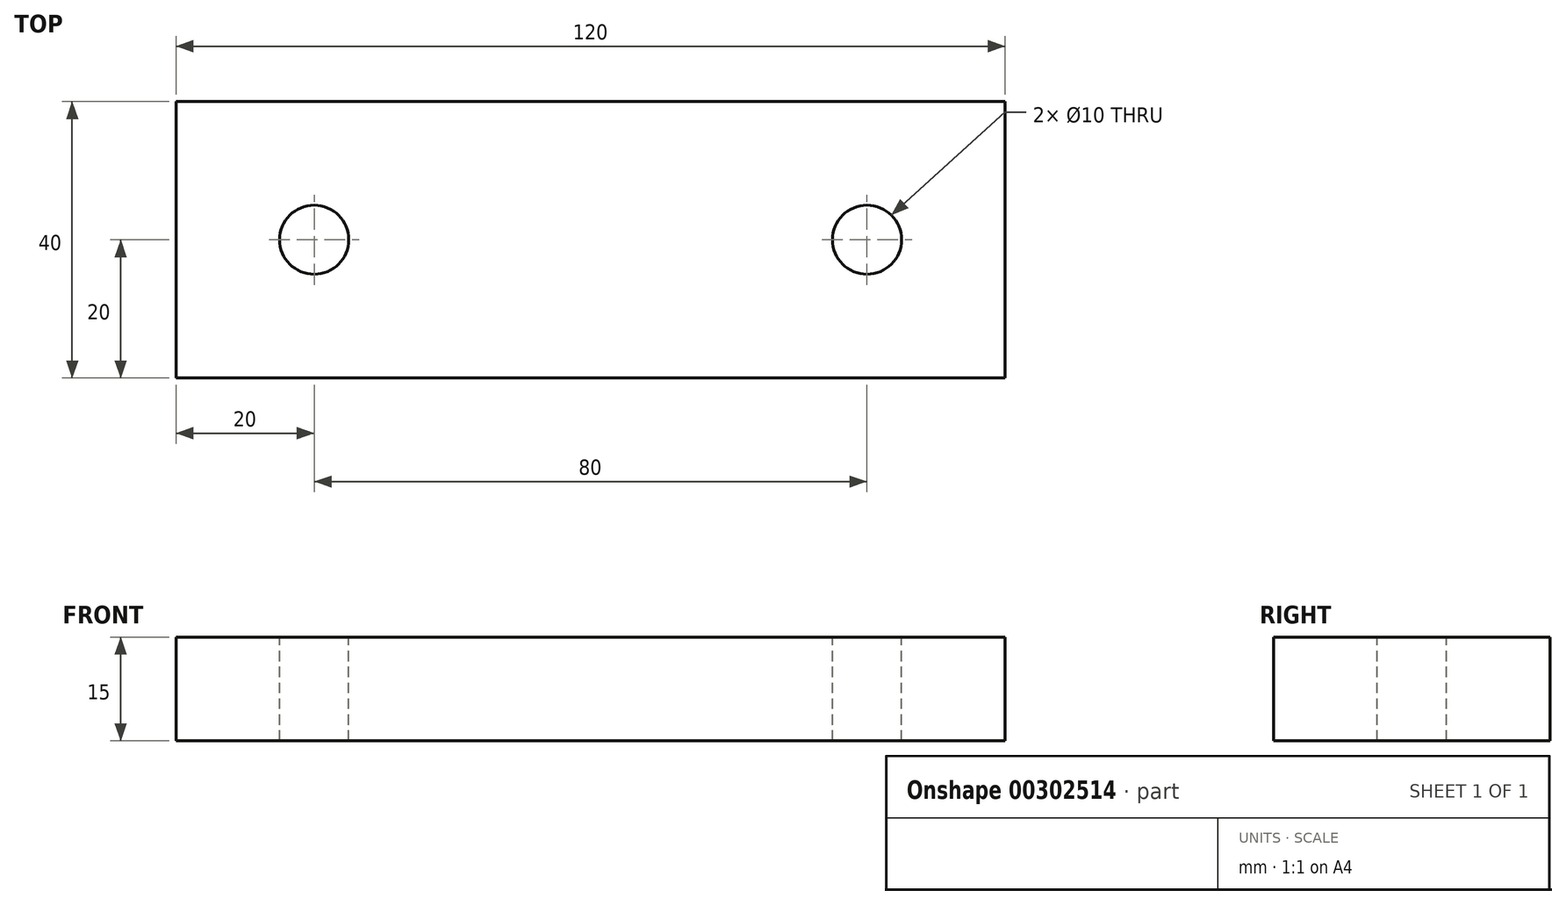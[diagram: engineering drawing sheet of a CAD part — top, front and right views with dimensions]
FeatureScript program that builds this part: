
annotation { "Feature Type Name" : "Feature", "Feature Type Description" : "" }
export const myFeature = defineFeature(function(context is Context, id is Id, definition is map)
    precondition{}
    {
        {
            var Q0;
            Q0=qCreatedBy(makeId("Front.planeOp"),FACE);
            var sketch = newSketch(context, id + "F0", { "sketchPlane" : qUnion([Q0])});
            skLineSegment(sketch, "E0", {"start": v(0, 0) * mm, "end": v(0, 15) * mm});
            skLineSegment(sketch, "E1", {"start": v(0, 15) * mm, "end": v(120, 15) * mm});
            skLineSegment(sketch, "E2", {"start": v(120, 15) * mm, "end": v(120, 0) * mm});
            skLineSegment(sketch, "E3", {"start": v(120, 0) * mm, "end": v(0, 0) * mm});
            skSolve(sketch);
        }
        {
            var Q0;
            Q0 = qSketchRegion(id + "F0", true);
            extrude(context, id + "F1", {"entities" : qUnion([Q0]), "depth" : 40 * mm});
        }
        {
            var Q0;
            Q0=makeQuery(id+"F1.opExtrude","SWEPT_FACE",FACE,{"disambiguationData":[OSD([sQuery(id+"F0.wireOp",EDGE,"E1")])]});
            var sketch = newSketch(context, id + "F2", { "sketchPlane" : qUnion([Q0])});
            skCircle(sketch, "E4", {"center": v(20, -20) * mm, "radius": 5 * mm});
            skCircle(sketch, "E5", {"center": v(100, -20) * mm, "radius": 5 * mm});
            skSolve(sketch);
        }
        {
            var Q0;
            Q0 = qSketchRegion(id + "F2", true);
            extrude(context, id + "F3", {"entities" : qUnion([Q0]), "operationType" : NewBodyOperationType.REMOVE, "endBound" : BoundingType.THROUGH_ALL, "oppositeDirection" : true, "depth" : 25 * mm});
        }
    });
